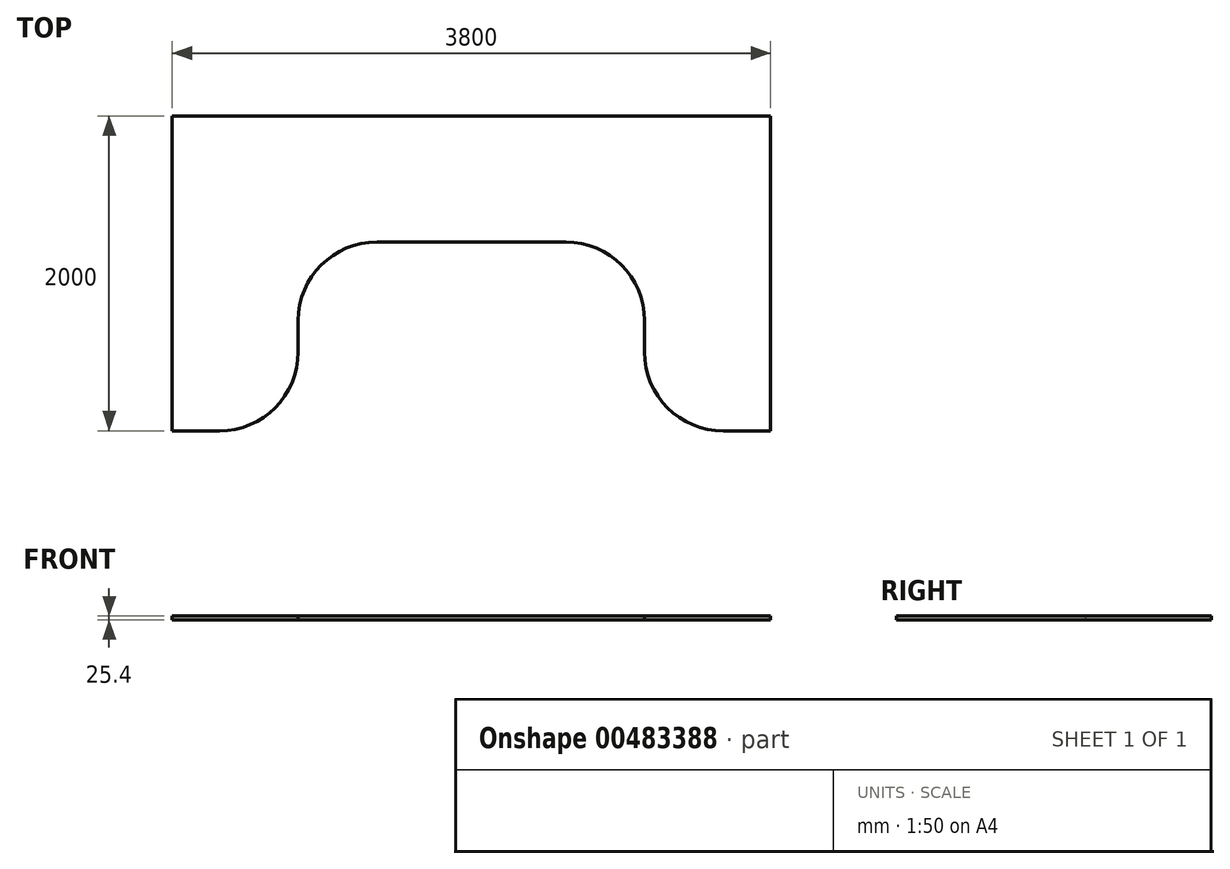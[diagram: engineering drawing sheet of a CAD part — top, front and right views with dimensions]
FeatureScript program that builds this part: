
annotation { "Feature Type Name" : "Feature", "Feature Type Description" : "" }
export const myFeature = defineFeature(function(context is Context, id is Id, definition is map)
    precondition{}
    {
        {
            var Q0;
            Q0=qCreatedBy(makeId("Top.planeOp"),FACE);
            var sketch = newSketch(context, id + "F0", { "sketchPlane" : qUnion([Q0])});
            skLineSegment(sketch, "E0", {"start": v(0, 0) * mm, "end": v(-3800, 0) * mm});
            skLineSegment(sketch, "E1", {"start": v(0, 0) * mm, "end": v(0, -2000) * mm});
            skLineSegment(sketch, "E2", {"start": v(-3800, 0) * mm, "end": v(-3800, -2000) * mm});
            skLineSegment(sketch, "E3", {"start": v(-3800, -2000) * mm, "end": v(-3500, -2000) * mm});
            skLineSegment(sketch, "E4", {"start": v(0, -2000) * mm, "end": v(-300, -2000) * mm});
            skLineSegment(sketch, "E5", {"start": v(-800, -1500) * mm, "end": v(-800, -1300) * mm});
            skLineSegment(sketch, "E6", {"start": v(-3000, -1500) * mm, "end": v(-3000, -1300) * mm});
            skLineSegment(sketch, "E7", {"start": v(-1300, -800) * mm, "end": v(-2500, -800) * mm});
            skPoint(sketch, "E8.visualSharp", {"position": v(-3000, -2000) * mm});
            skArc(sketch, "E8.filletArc", {"start": v(-3006.35, -2000) * mm, "mid": v(-3001.86, -1998.14) * mm, "end": v(-3000, -1993.65) * mm});
            skArc(sketch, "E9.filletArc", {"start": v(-3500, -2000) * mm, "mid": v(-3146.45, -1853.55) * mm, "end": v(-3000, -1500) * mm});
            skPoint(sketch, "E10.visualSharp", {"position": v(-3000, -800) * mm});
            skArc(sketch, "E10.filletArc", {"start": v(-2500, -800) * mm, "mid": v(-2853.55, -946.45) * mm, "end": v(-3000, -1300) * mm});
            skPoint(sketch, "E11.visualSharp", {"position": v(-800, -800) * mm});
            skArc(sketch, "E11.filletArc", {"start": v(-800, -1300) * mm, "mid": v(-946.45, -946.45) * mm, "end": v(-1300, -800) * mm});
            skPoint(sketch, "E12.visualSharp", {"position": v(-800, -2000) * mm});
            skArc(sketch, "E12.filletArc", {"start": v(-800, -1500) * mm, "mid": v(-653.55, -1853.55) * mm, "end": v(-300, -2000) * mm});
            skSolve(sketch);
        }
        {
            var Q0;
            Q0=makeQuery(id+"F0.imprint","IMPRINT",FACE,{"disambiguationData":[TD([[makeQuery(id+"F0.imprint","IMPRINT",EDGE,{"derivedFrom":sQuery(id+"F0.wireOp",EDGE,"E0")}),1.0]])]});
            extrude(context, id + "F1", {"entities" : qUnion([Q0]), "depth" : 25.4 * mm});
        }
    });
